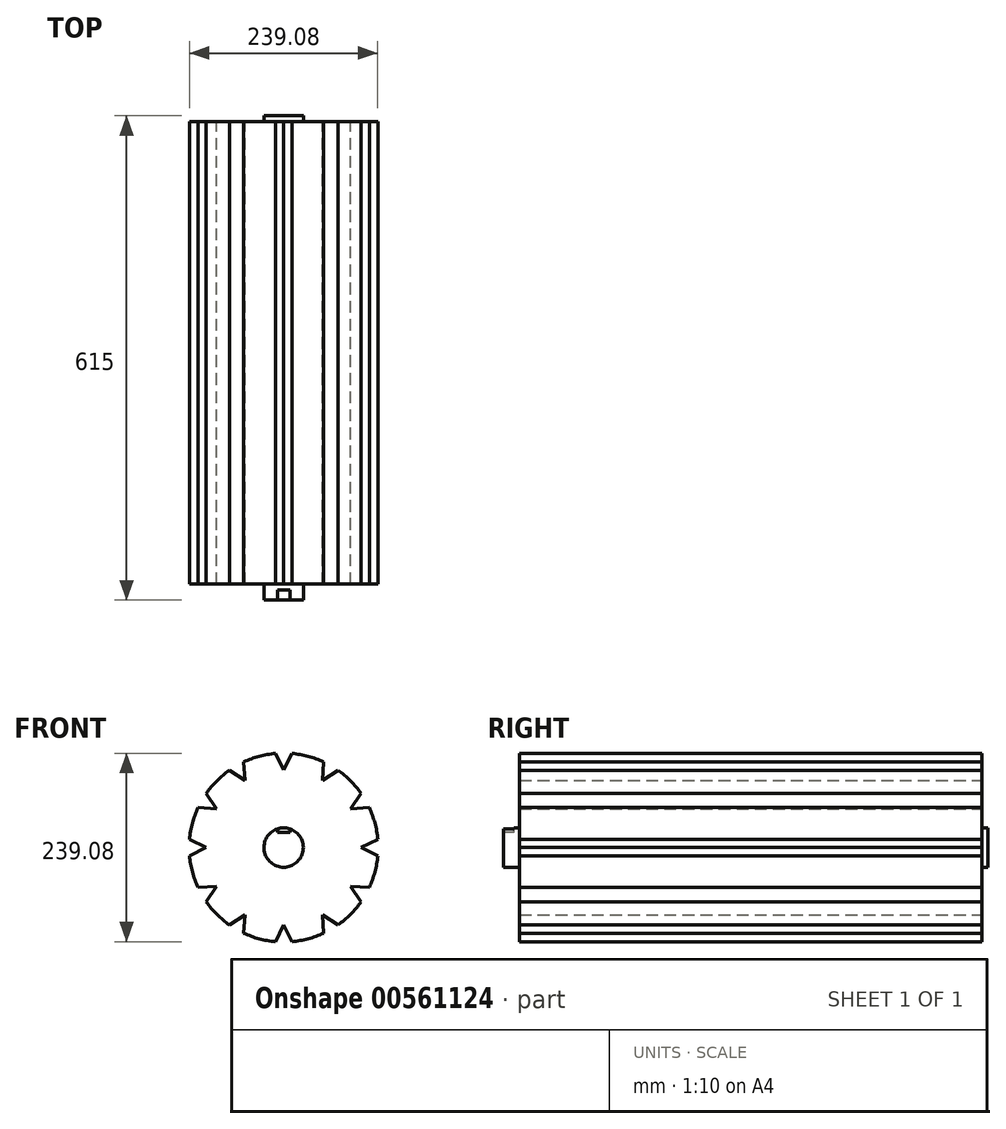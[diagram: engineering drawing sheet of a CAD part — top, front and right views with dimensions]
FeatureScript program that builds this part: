
annotation { "Feature Type Name" : "Feature", "Feature Type Description" : "" }
export const myFeature = defineFeature(function(context is Context, id is Id, definition is map)
    precondition{}
    {
        {
            var Q0;
            Q0=qCreatedBy(makeId("Front.planeOp"),FACE);
            var sketch = newSketch(context, id + "F0", { "sketchPlane" : qUnion([Q0])});
            skCircle(sketch, "E0", {"center": v(0, 0) * mm, "radius": 120 * mm});
            skLineSegment(sketch, "E1", {"start": v(-10.47, 119.54) * mm, "end": v(0, 98.4) * mm});
            skLineSegment(sketch, "E2", {"start": v(0, 0) * mm, "end": v(0, 240.15) * mm, "construction": true});
            skLineSegment(sketch, "E3.MirrorCS", {"start": v(10.47, 119.54) * mm, "end": v(0, 98.4) * mm});
            skLineSegment(sketch, "E4.1.1", {"start": v(-68.84, 98.3) * mm, "end": v(-49.2, 85.22) * mm});
            skLineSegment(sketch, "E4.1.2", {"start": v(0, 0) * mm, "end": v(-120.08, 207.98) * mm, "construction": true});
            skLineSegment(sketch, "E4.1.3", {"start": v(-50.7, 108.76) * mm, "end": v(-49.2, 85.22) * mm});
            skLineSegment(sketch, "E4.2.1", {"start": v(-108.76, 50.7) * mm, "end": v(-85.22, 49.2) * mm});
            skLineSegment(sketch, "E4.2.2", {"start": v(0, 0) * mm, "end": v(-207.98, 120.08) * mm, "construction": true});
            skLineSegment(sketch, "E4.2.3", {"start": v(-98.3, 68.84) * mm, "end": v(-85.22, 49.2) * mm});
            skLineSegment(sketch, "E4.3.1", {"start": v(-119.54, -10.47) * mm, "end": v(-98.4, 0) * mm});
            skLineSegment(sketch, "E4.3.2", {"start": v(0, 0) * mm, "end": v(-240.15, 0) * mm, "construction": true});
            skLineSegment(sketch, "E4.3.3", {"start": v(-119.54, 10.47) * mm, "end": v(-98.4, 0) * mm});
            skLineSegment(sketch, "E4.4.1", {"start": v(-98.3, -68.84) * mm, "end": v(-85.22, -49.2) * mm});
            skLineSegment(sketch, "E4.4.2", {"start": v(0, 0) * mm, "end": v(-207.98, -120.08) * mm, "construction": true});
            skLineSegment(sketch, "E4.4.3", {"start": v(-108.76, -50.7) * mm, "end": v(-85.22, -49.2) * mm});
            skLineSegment(sketch, "E4.5.1", {"start": v(-50.7, -108.76) * mm, "end": v(-49.2, -85.22) * mm});
            skLineSegment(sketch, "E4.5.2", {"start": v(0, 0) * mm, "end": v(-120.08, -207.98) * mm, "construction": true});
            skLineSegment(sketch, "E4.5.3", {"start": v(-68.84, -98.3) * mm, "end": v(-49.2, -85.22) * mm});
            skLineSegment(sketch, "E4.6.1", {"start": v(10.47, -119.54) * mm, "end": v(0, -98.4) * mm});
            skLineSegment(sketch, "E4.6.2", {"start": v(0, 0) * mm, "end": v(0, -240.15) * mm, "construction": true});
            skLineSegment(sketch, "E4.6.3", {"start": v(-10.47, -119.54) * mm, "end": v(0, -98.4) * mm});
            skLineSegment(sketch, "E4.7.1", {"start": v(68.84, -98.3) * mm, "end": v(49.2, -85.22) * mm});
            skLineSegment(sketch, "E4.7.2", {"start": v(0, 0) * mm, "end": v(120.08, -207.98) * mm, "construction": true});
            skLineSegment(sketch, "E4.7.3", {"start": v(50.7, -108.76) * mm, "end": v(49.2, -85.22) * mm});
            skLineSegment(sketch, "E4.8.1", {"start": v(108.76, -50.7) * mm, "end": v(85.22, -49.2) * mm});
            skLineSegment(sketch, "E4.8.2", {"start": v(0, 0) * mm, "end": v(207.98, -120.08) * mm, "construction": true});
            skLineSegment(sketch, "E4.8.3", {"start": v(98.3, -68.84) * mm, "end": v(85.22, -49.2) * mm});
            skLineSegment(sketch, "E4.9.1", {"start": v(119.54, 10.47) * mm, "end": v(98.4, 0) * mm});
            skLineSegment(sketch, "E4.9.2", {"start": v(0, 0) * mm, "end": v(240.15, 0) * mm, "construction": true});
            skLineSegment(sketch, "E4.9.3", {"start": v(119.54, -10.47) * mm, "end": v(98.4, 0) * mm});
            skLineSegment(sketch, "E4.10.1", {"start": v(98.3, 68.84) * mm, "end": v(85.22, 49.2) * mm});
            skLineSegment(sketch, "E4.10.2", {"start": v(0, 0) * mm, "end": v(207.98, 120.08) * mm, "construction": true});
            skLineSegment(sketch, "E4.10.3", {"start": v(108.76, 50.7) * mm, "end": v(85.22, 49.2) * mm});
            skLineSegment(sketch, "E4.11.1", {"start": v(50.7, 108.76) * mm, "end": v(49.2, 85.22) * mm});
            skLineSegment(sketch, "E4.11.2", {"start": v(0, 0) * mm, "end": v(120.08, 207.98) * mm, "construction": true});
            skLineSegment(sketch, "E4.11.3", {"start": v(68.84, 98.3) * mm, "end": v(49.2, 85.22) * mm});
            skSolve(sketch);
        }
        {
            var Q0;
            {var subQ15=sQuery(id+"F0.wireOp",EDGE,"E1");Q0=makeQuery(id+"F0.imprint","IMPRINT",FACE,{"disambiguationData":[TD([[makeQuery(id+"F0.imprint","IMPRINT",EDGE,{"derivedFrom":subQ15}),-1.0]])]});}
            extrude(context, id + "F1", {"entities" : qUnion([Q0]), "depth" : 587.5 * mm, "offsetDistance" : 25.4 * mm});
        }
        {
            var Q0;
            Q0=makeQuery(id+"F1.opExtrude","CAP_FACE",FACE,{"disambiguationData":[OSD([sQuery(id+"F0.wireOp",EDGE,"E1"),sQuery(id+"F0.wireOp",EDGE,"E3.MirrorCS"),sQuery(id+"F0.wireOp",EDGE,"E4.1.1"),sQuery(id+"F0.wireOp",EDGE,"E4.1.3"),sQuery(id+"F0.wireOp",EDGE,"E4.2.1"),sQuery(id+"F0.wireOp",EDGE,"E4.2.3"),sQuery(id+"F0.wireOp",EDGE,"E4.3.1"),sQuery(id+"F0.wireOp",EDGE,"E4.3.3"),sQuery(id+"F0.wireOp",EDGE,"E4.4.1"),sQuery(id+"F0.wireOp",EDGE,"E4.4.3"),sQuery(id+"F0.wireOp",EDGE,"E4.5.1"),sQuery(id+"F0.wireOp",EDGE,"E4.5.3"),sQuery(id+"F0.wireOp",EDGE,"E4.6.1"),sQuery(id+"F0.wireOp",EDGE,"E4.6.3"),sQuery(id+"F0.wireOp",EDGE,"E4.7.1"),sQuery(id+"F0.wireOp",EDGE,"E4.7.3"),sQuery(id+"F0.wireOp",EDGE,"E4.8.1"),sQuery(id+"F0.wireOp",EDGE,"E4.8.3"),sQuery(id+"F0.wireOp",EDGE,"E4.9.1"),sQuery(id+"F0.wireOp",EDGE,"E4.9.3"),sQuery(id+"F0.wireOp",EDGE,"E4.10.1"),sQuery(id+"F0.wireOp",EDGE,"E4.10.3"),sQuery(id+"F0.wireOp",EDGE,"E0"),sQuery(id+"F0.wireOp",EDGE,"E4.11.1"),sQuery(id+"F0.wireOp",EDGE,"E4.11.3")])],"isStart":true});
            var sketch = newSketch(context, id + "F2", { "sketchPlane" : qUnion([Q0])});
            skPoint(sketch, "E5", {"position": v(0, 0) * mm});
            skCircle(sketch, "E6", {"center": v(0, 0) * mm, "radius": 25 * mm});
            skSolve(sketch);
        }
        {
            var Q0;
            Q0 = qSketchRegion(id + "F2", true);
            extrude(context, id + "F3", {"entities" : qUnion([Q0]), "operationType" : NewBodyOperationType.ADD, "depth" : 7.5 * mm, "offsetDistance" : 25.4 * mm});
        }
        {
            var Q0;
            Q0=makeQuery(id+"F1.opExtrude","CAP_FACE",FACE,{"disambiguationData":[OSD([sQuery(id+"F0.wireOp",EDGE,"E1"),sQuery(id+"F0.wireOp",EDGE,"E3.MirrorCS"),sQuery(id+"F0.wireOp",EDGE,"E4.1.1"),sQuery(id+"F0.wireOp",EDGE,"E4.1.3"),sQuery(id+"F0.wireOp",EDGE,"E4.2.1"),sQuery(id+"F0.wireOp",EDGE,"E4.2.3"),sQuery(id+"F0.wireOp",EDGE,"E4.3.1"),sQuery(id+"F0.wireOp",EDGE,"E4.3.3"),sQuery(id+"F0.wireOp",EDGE,"E4.4.1"),sQuery(id+"F0.wireOp",EDGE,"E4.4.3"),sQuery(id+"F0.wireOp",EDGE,"E4.5.1"),sQuery(id+"F0.wireOp",EDGE,"E4.5.3"),sQuery(id+"F0.wireOp",EDGE,"E4.6.1"),sQuery(id+"F0.wireOp",EDGE,"E4.6.3"),sQuery(id+"F0.wireOp",EDGE,"E4.7.1"),sQuery(id+"F0.wireOp",EDGE,"E4.7.3"),sQuery(id+"F0.wireOp",EDGE,"E4.8.1"),sQuery(id+"F0.wireOp",EDGE,"E4.8.3"),sQuery(id+"F0.wireOp",EDGE,"E4.9.1"),sQuery(id+"F0.wireOp",EDGE,"E4.9.3"),sQuery(id+"F0.wireOp",EDGE,"E4.10.1"),sQuery(id+"F0.wireOp",EDGE,"E4.10.3"),sQuery(id+"F0.wireOp",EDGE,"E0"),sQuery(id+"F0.wireOp",EDGE,"E4.11.1"),sQuery(id+"F0.wireOp",EDGE,"E4.11.3")])],"isStart":false});
            var sketch = newSketch(context, id + "F4", { "sketchPlane" : qUnion([Q0])});
            skCircle(sketch, "E7", {"center": v(0, 0) * mm, "radius": 25 * mm});
            skSolve(sketch);
        }
        {
            var Q0;
            Q0=makeQuery(id+"F4.imprint","IMPRINT",FACE,{"disambiguationData":[TD([[makeQuery(id+"F4.imprint","IMPRINT",EDGE,{"derivedFrom":sQuery(id+"F4.wireOp",EDGE,"E7")}),1.0]])]});
            extrude(context, id + "F5", {"entities" : qUnion([Q0]), "operationType" : NewBodyOperationType.ADD, "depth" : 20 * mm, "offsetDistance" : 25.4 * mm});
        }
        {
            var Q0;
            Q0=makeQuery(id+"F5.opExtrude","CAP_FACE",FACE,{"disambiguationData":[OSD([sQuery(id+"F4.wireOp",EDGE,"E7")])],"isStart":false});
            var sketch = newSketch(context, id + "F6", { "sketchPlane" : qUnion([Q0])});
            skLineSegment(sketch, "E8.bottom", {"start": v(-8, 19) * mm, "end": v(8, 19) * mm});
            skLineSegment(sketch, "E8.top", {"start": v(-8, 26) * mm, "end": v(8, 26) * mm});
            skLineSegment(sketch, "E8.left", {"start": v(-8, 19) * mm, "end": v(-8, 26) * mm});
            skLineSegment(sketch, "E8.right", {"start": v(8, 19) * mm, "end": v(8, 26) * mm});
            skSolve(sketch);
        }
        {
            var Q0;
            Q0 = qSketchRegion(id + "F6", true);
            extrude(context, id + "F7", {"entities" : qUnion([Q0]), "operationType" : NewBodyOperationType.REMOVE, "oppositeDirection" : true, "depth" : 13 * mm, "offsetDistance" : 25.4 * mm});
        }
    });
